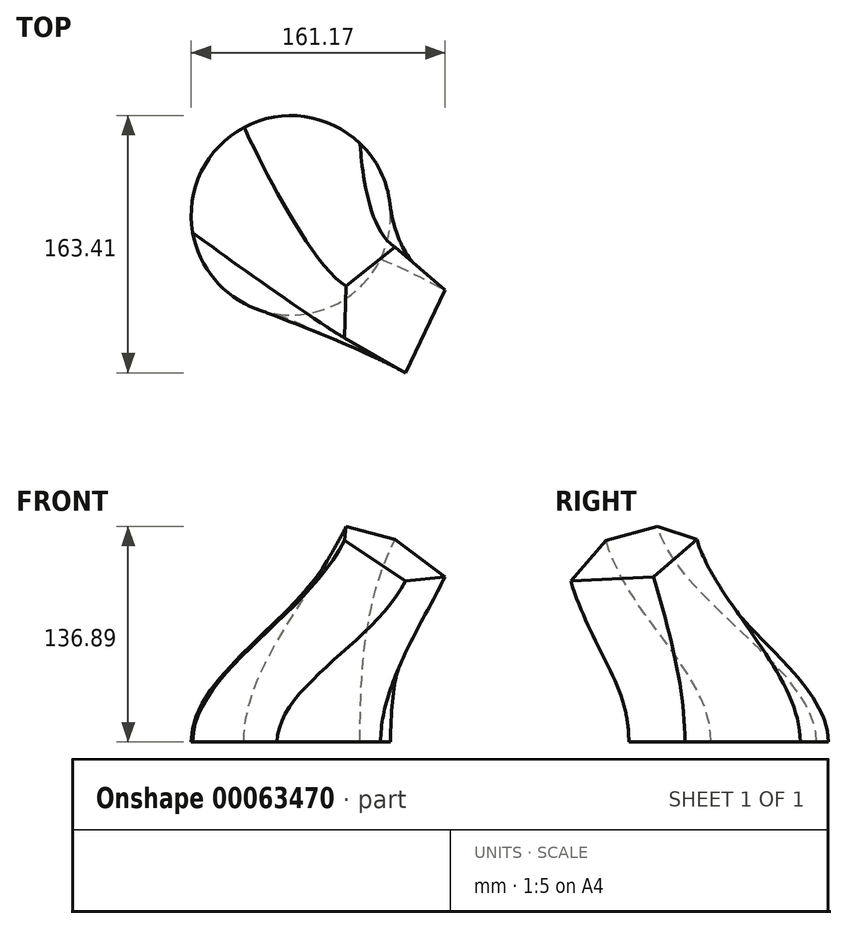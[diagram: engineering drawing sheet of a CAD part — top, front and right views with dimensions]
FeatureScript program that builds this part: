
annotation { "Feature Type Name" : "Feature", "Feature Type Description" : "" }
export const myFeature = defineFeature(function(context is Context, id is Id, definition is map)
    precondition{}
    {
        {
            var Q0;
            Q0=qCreatedBy(makeId("Top.planeOp"),FACE);
            var sketch = newSketch(context, id + "F0", { "sketchPlane" : qUnion([Q0])});
            skCircle(sketch, "E0", {"center": v(0, 0) * mm, "radius": 63.33 * mm});
            skSolve(sketch);
        }
        {
            var Q0;
            Q0=qCreatedBy(makeId("Top.planeOp"),FACE);
            cPlane(context, id + "F1", {"entities" : qUnion([Q0]), "cplaneType" : CPlaneType.OFFSET, "offset" : 150 * mm, "width" : 150 * mm, "height" : 150 * mm});
        }
        {
            var Q0;
            Q0=qCreatedBy(id+"F1.planeOp",FACE);
            var sketch = newSketch(context, id + "F2", { "sketchPlane" : qUnion([Q0])});
            skLineSegment(sketch, "E1", {"start": v(48.16, 22.66) * mm, "end": v(7.57, -47.24) * mm});
            skSolve(sketch);
        }
        {
            var Q0;
            Q0=sQuery(id+"F2.wireOp",EDGE,"E1");
            cPlane(context, id + "F3", {"entities" : qUnion([Q0]), "cplaneType" : CPlaneType.LINE_ANGLE, "offset" : 150 * mm, "angle" : 330 * degree, "width" : 150 * mm, "height" : 150 * mm});
        }
        {
            var Q0;
            Q0=qCreatedBy(id+"F3.planeOp",FACE);
            var sketch = newSketch(context, id + "F4", { "sketchPlane" : qUnion([Q0])});
            skCircle(sketch, "E2.cCircle", {"center": v(0, 22.8) * mm, "radius": 31.24 * mm, "construction": true});
            skLineSegment(sketch, "E2.0", {"start": v(38.96, 16.5) * mm, "end": v(3.76, -16.5) * mm});
            skLineSegment(sketch, "E2.1", {"start": v(3.76, -16.5) * mm, "end": v(-30.63, 5.17) * mm});
            skLineSegment(sketch, "E2.2", {"start": v(-30.63, 5.17) * mm, "end": v(-31.84, 39.15) * mm});
            skLineSegment(sketch, "E2.3", {"start": v(-31.84, 39.15) * mm, "end": v(11.17, 67.68) * mm});
            skLineSegment(sketch, "E2.4", {"start": v(11.17, 67.68) * mm, "end": v(38.96, 16.5) * mm});
            skPoint(sketch, "E2.0.midPoint", {"position": v(21.36, 0) * mm});
            skSolve(sketch);
        }
        {
            var Q0;
            Q0=makeQuery(id+"F0.imprint","IMPRINT",FACE,{"disambiguationData":[TD([[makeQuery(id+"F0.imprint","IMPRINT",EDGE,{"derivedFrom":sQuery(id+"F0.wireOp",EDGE,"E0")}),1.0]])]});
            var Q1;
            Q1=makeQuery(id+"F4.imprint","IMPRINT",FACE,{"disambiguationData":[TD([[makeQuery(id+"F4.imprint","IMPRINT",EDGE,{"derivedFrom":sQuery(id+"F4.wireOp",EDGE,"E2.0")}),-1.0]])]});
            loft(context, id + "F5", {"startCondition" : LoftEndDerivativeType.NORMAL_TO_PROFILE, "startMagnitude" : 1, "endCondition" : LoftEndDerivativeType.NORMAL_TO_PROFILE, "endMagnitude" : 1, "sheetProfilesArray" : [{ "sheetProfileEntities" : qUnion([Q0]) }, { "sheetProfileEntities" : qUnion([Q1]) }]});
        }
    });
